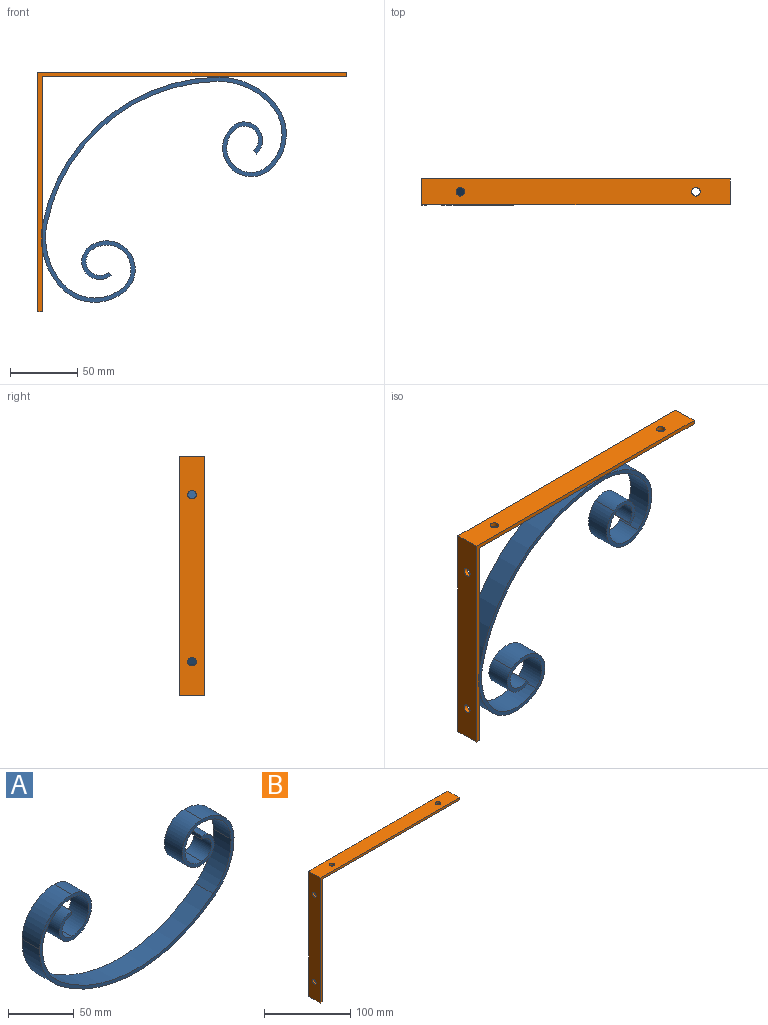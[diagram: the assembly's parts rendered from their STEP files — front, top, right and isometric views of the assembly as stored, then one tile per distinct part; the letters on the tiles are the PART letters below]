
ASSEMBLY  parts=2 mates=2
PART A: 22 faces, bbox 209.6x19.1x107.6 mm
  f0: cylinder r=131.46mm len=164.66mm, axis (0,1,0), area 3389.7mm2, adj f1,f19,f20,f21
  f1: cylinder r=51.59mm len=41.28mm, axis (0,1,0), area 898.8mm2, adj f0,f2,f20,f21
  f2: cylinder r=31.6mm len=31.59mm, axis (0,1,0), area 933.3mm2, adj f1,f3,f20,f21
  f3: cylinder r=18.06mm len=36.12mm, axis (0,1,0), area 1080.7mm2, adj f2,f4,f20,f21
  f4: cylinder r=10.32mm len=20.64mm, axis (0,1,0), area 617.5mm2, adj f3,f5,f20,f21
  f5: plane 19.05x3.18mm, normal (1,0,0), area 60.5mm2, adj f4,f6,f20,f21
  f6: cylinder r=13.49mm len=26.99mm, axis (0,1,0), area 807.6mm2, adj f5,f7,f20,f21
  f7: cylinder r=21.23mm len=42.47mm, axis (0,1,0), area 1270.7mm2, adj f6,f8,f20,f21
  f8: cylinder r=34.78mm len=34.77mm, axis (0,1,0), area 1027.1mm2, adj f7,f9,f20,f21
  f9: cylinder r=54.77mm len=43.82mm, axis (0,1,0), area 954.1mm2, adj f8,f10,f20,f21
  f10: cylinder r=134.63mm len=168.64mm, axis (0,1,0), area 3471.5mm2, adj f9,f11,f20,f21
  f11: cylinder r=54.77mm len=43.82mm, axis (0,1,0), area 954.1mm2, adj f10,f12,f20,f21
  f12: cylinder r=34.78mm len=34.77mm, axis (0,1,0), area 1027.1mm2, adj f11,f13,f20,f21
  f13: cylinder r=21.23mm len=42.47mm, axis (0,1,0), area 1270.7mm2, adj f12,f14,f20,f21
  f14: cylinder r=13.49mm len=26.99mm, axis (0,1,0), area 807.6mm2, adj f13,f15,f20,f21
  f15: plane 19.05x3.18mm, normal (-1,0,0), area 60.5mm2, adj f14,f16,f20,f21
  f16: cylinder r=10.32mm len=20.64mm, axis (0,1,0), area 617.5mm2, adj f15,f17,f20,f21
  f17: cylinder r=18.06mm len=36.12mm, axis (0,1,0), area 1080.7mm2, adj f16,f18,f20,f21
  f18: cylinder r=31.6mm len=31.59mm, axis (0,1,0), area 933.3mm2, adj f17,f19,f20,f21
  f19: cylinder r=51.59mm len=41.28mm, axis (0,1,0), area 898.8mm2, adj f0,f18,f20,f21
  f20: plane 209.57x107.56mm, normal (0,-1,0), area 1836.7mm2, adj f0,f1,f2,f3,f4,f5,f6,f7
  f21: plane 209.57x107.56mm, normal (0,1,0), area 1836.7mm2, adj f0,f1,f2,f3,f4,f5,f6,f7
PART B: 12 faces, bbox 228.6x19.1x177.8 mm
  f0: plane 177.8x19.05mm, normal (-1,0,0), area 3323.8mm2, adj f1,f5,f6,f7,f8,f9
  f1: plane 19.05x3.18mm, normal (0,0,-1), area 60.5mm2, adj f0,f2,f6,f7
  f2: plane 174.63x19.05mm, normal (1,0,0), area 3263.3mm2, adj f1,f3,f6,f7,f8,f9
  f3: plane 225.43x19.05mm, normal (0,0,-1), area 4231mm2, adj f2,f4,f6,f7,f10,f11
  f4: plane 19.05x3.18mm, normal (1,0,0), area 60.5mm2, adj f3,f5,f6,f7
  f5: plane 228.6x19.05mm, normal (0,0,1), area 4291.5mm2, adj f0,f4,f6,f7,f10,f11
  f6: plane 228.6x177.8mm, normal (0,-1,0), area 1280.2mm2, adj f0,f1,f2,f3,f4,f5
  f7: plane 228.6x177.8mm, normal (0,1,0), area 1280.2mm2, adj f0,f1,f2,f3,f4,f5
  f8: cylinder r=3.17mm len=6.35mm, axis (1,0,0), area 63.3mm2, adj f0,f2
  f9: cylinder r=3.17mm len=6.35mm, axis (1,0,0), area 63.3mm2, adj f0,f2
  f10: cylinder r=3.17mm len=6.35mm, axis (0,0,-1), area 63.3mm2, adj f3,f5
  f11: cylinder r=3.17mm len=6.35mm, axis (0,0,-1), area 63.3mm2, adj f3,f5
PLACE A rot(axis=(0,1,0),140deg) t=(62.02,18.56,79.15)mm
PLACE B rot(axis=(0,1,0),0deg) t=(-67.17,18.56,-76.91)mm
MATE parallel A.f20 <-> B.f6  axis (0,-1,0) through (18.85,-0.49,21.7)mm
MATE parallel B.f6 <-> A.f20  axis (0,-1,0) through (-1.68,-0.49,60.81)mm
